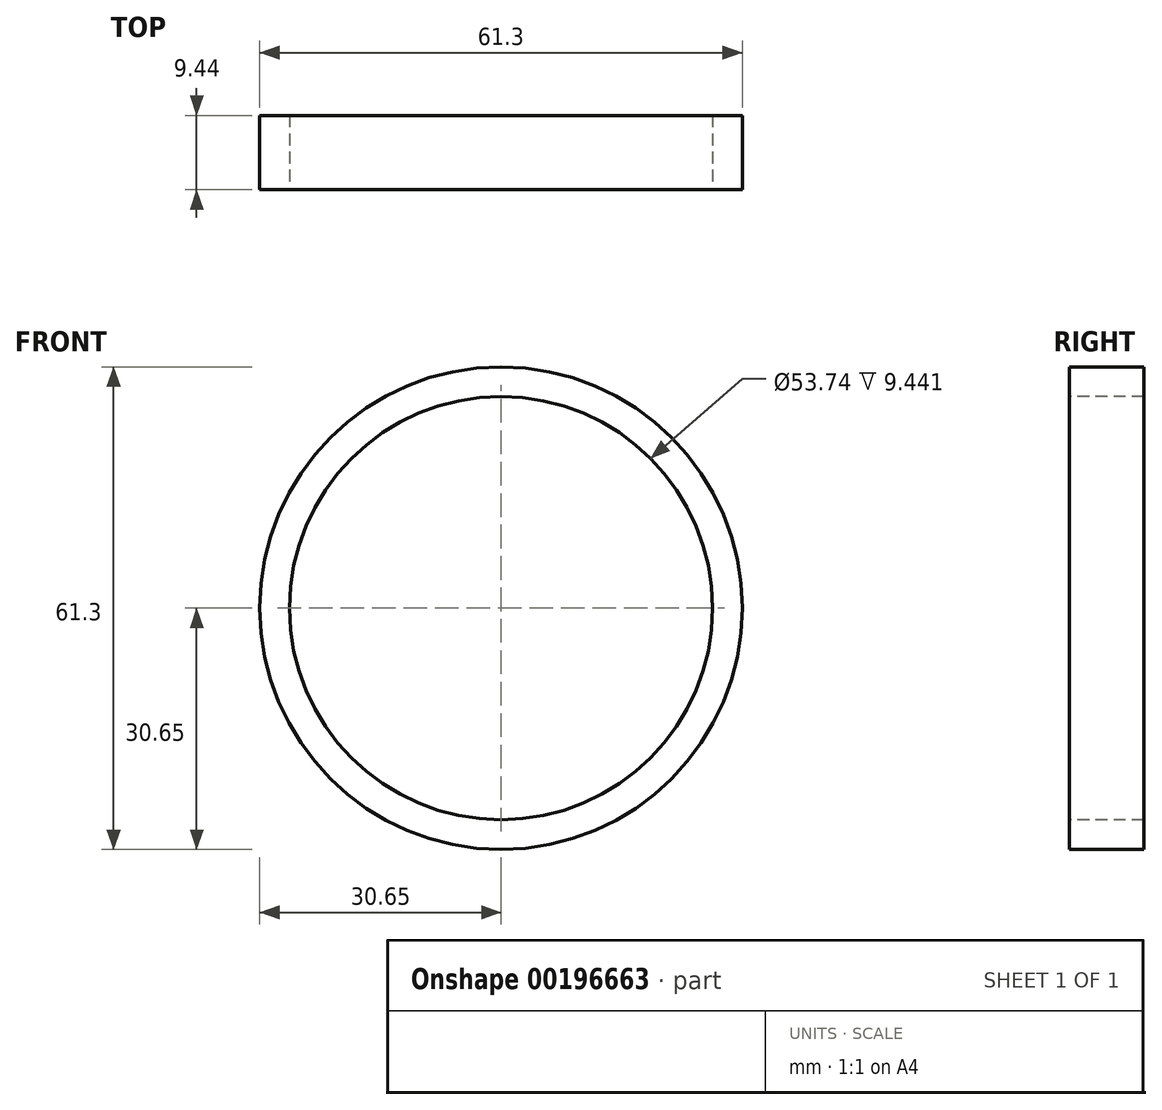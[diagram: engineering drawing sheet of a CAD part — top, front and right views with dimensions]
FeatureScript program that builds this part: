
annotation { "Feature Type Name" : "Feature", "Feature Type Description" : "" }
export const myFeature = defineFeature(function(context is Context, id is Id, definition is map)
    precondition{}
    {
        {
            var Q0;
            Q0=qCreatedBy(makeId("Front.planeOp"),FACE);
            var sketch = newSketch(context, id + "F0", { "sketchPlane" : qUnion([Q0])});
            skCircle(sketch, "E0", {"center": v(0, 0) * mm, "radius": 28.76 * mm});
            skSolve(sketch);
        }
        {
            var Q0;
            Q0=qCreatedBy(makeId("Top.planeOp"),FACE);
            var sketch = newSketch(context, id + "F1", { "sketchPlane" : qUnion([Q0])});
            skLineSegment(sketch, "E1.0", {"start": v(28.76, 0) * mm, "end": v(-28.76, 0) * mm});
            skLineSegment(sketch, "E2.bottom", {"start": v(-26.87, 4.72) * mm, "end": v(-30.65, 4.72) * mm});
            skLineSegment(sketch, "E2.top", {"start": v(-26.87, -4.72) * mm, "end": v(-30.65, -4.72) * mm});
            skLineSegment(sketch, "E2.left", {"start": v(-26.87, 4.72) * mm, "end": v(-26.87, -4.72) * mm});
            skLineSegment(sketch, "E2.right", {"start": v(-30.65, 4.72) * mm, "end": v(-30.65, -4.72) * mm});
            skPoint(sketch, "E2.middle", {"position": v(-28.76, 0) * mm});
            skSolve(sketch);
        }
        {
            var Q0;
            {var subQ0=sQuery(id+"F1.wireOp",EDGE,"E2.bottom");Q0=makeQuery(id+"F1.imprint","IMPRINT",FACE,{"disambiguationData":[TD([[makeQuery(id+"F1.imprint","IMPRINT",EDGE,{"derivedFrom":subQ0}),1.0]])]});}
            var Q1;
            Q1=sQuery(id+"F0.wireOp",EDGE,"E0");
            sweep(context, id + "F2", {"profiles" : qUnion([Q0]), "path" : qUnion([Q1])});
        }
    });
